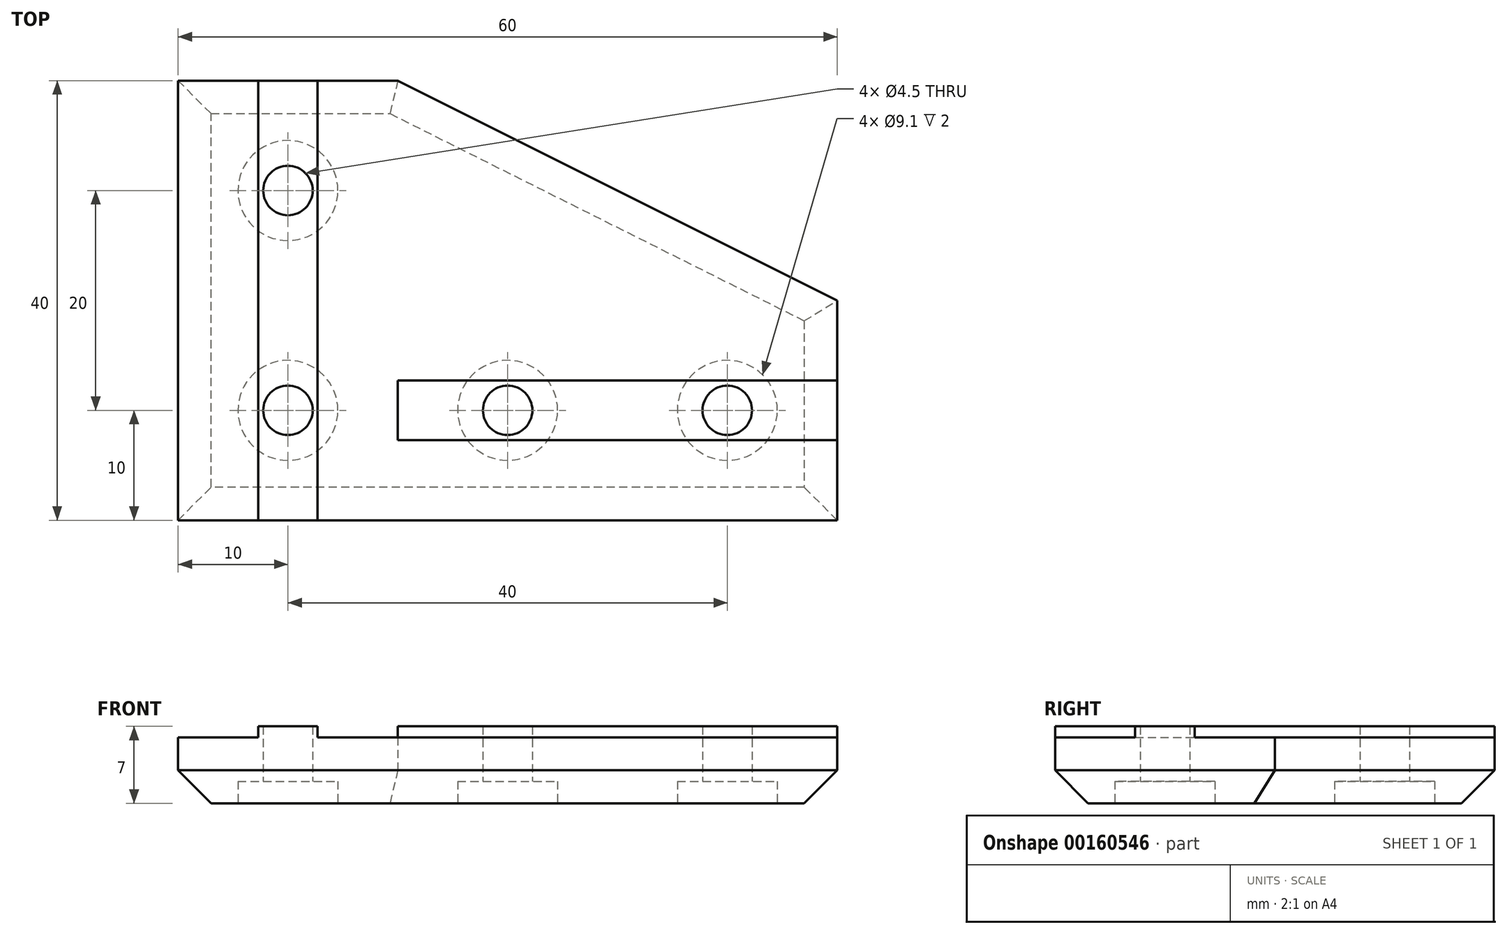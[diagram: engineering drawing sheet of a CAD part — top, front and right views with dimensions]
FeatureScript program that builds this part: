
annotation { "Feature Type Name" : "Feature", "Feature Type Description" : "" }
export const myFeature = defineFeature(function(context is Context, id is Id, definition is map)
    precondition{}
    {
        {
            var Q0;
            Q0=qCreatedBy(makeId("Top.planeOp"),FACE);
            var sketch = newSketch(context, id + "F0", { "sketchPlane" : qUnion([Q0])});
            skLineSegment(sketch, "E0", {"start": v(0, 0) * mm, "end": v(0, 40) * mm});
            skLineSegment(sketch, "E1", {"start": v(0, 40) * mm, "end": v(20, 40) * mm});
            skLineSegment(sketch, "E2", {"start": v(20, 40) * mm, "end": v(20, 20) * mm, "construction": true});
            skLineSegment(sketch, "E3", {"start": v(20, 20) * mm, "end": v(60, 20) * mm, "construction": true});
            skLineSegment(sketch, "E4", {"start": v(60, 20) * mm, "end": v(60, 0) * mm});
            skLineSegment(sketch, "E5", {"start": v(60, 0) * mm, "end": v(0, 0) * mm});
            skLineSegment(sketch, "E6", {"start": v(20, 40) * mm, "end": v(60, 20) * mm});
            skSolve(sketch);
        }
        {
            var Q0;
            Q0=qSketchRegion(id+"F0",true);
            extrude(context, id + "F1", {"entities" : qUnion([Q0]), "depth" : 6 * mm});
        }
        {
            var Q0;
            Q0=makeQuery(id+"F1.opExtrude","CAP_FACE",FACE,{"disambiguationData":[OSD([sQuery(id+"F0.wireOp",EDGE,"E0"),sQuery(id+"F0.wireOp",EDGE,"E1"),sQuery(id+"F0.wireOp",EDGE,"E2"),sQuery(id+"F0.wireOp",EDGE,"E3"),sQuery(id+"F0.wireOp",EDGE,"E4"),sQuery(id+"F0.wireOp",EDGE,"E5")])],"isStart":false});
            var sketch = newSketch(context, id + "F2", { "sketchPlane" : qUnion([Q0])});
            skLineSegment(sketch, "E7", {"start": v(7.3, 40) * mm, "end": v(12.71, 40) * mm});
            skLineSegment(sketch, "E8", {"start": v(12.71, 40) * mm, "end": v(12.71, 0) * mm});
            skLineSegment(sketch, "E9", {"start": v(12.71, 0) * mm, "end": v(10, 0) * mm});
            skPoint(sketch, "E9.endSnap0", {"position": v(10, 40) * mm});
            skLineSegment(sketch, "E10", {"start": v(10, 0) * mm, "end": v(7.3, 0) * mm});
            skLineSegment(sketch, "E11", {"start": v(7.3, 0) * mm, "end": v(7.3, 40) * mm});
            skLineSegment(sketch, "E12", {"start": v(60, 12.7) * mm, "end": v(60, 7.3) * mm});
            skLineSegment(sketch, "E13", {"start": v(60, 7.3) * mm, "end": v(20, 7.3) * mm});
            skLineSegment(sketch, "E14", {"start": v(20, 7.3) * mm, "end": v(20, 10) * mm});
            skPoint(sketch, "E14.endSnap0", {"position": v(60, 10) * mm});
            skLineSegment(sketch, "E15", {"start": v(20, 10) * mm, "end": v(20, 12.71) * mm});
            skLineSegment(sketch, "E16", {"start": v(20, 12.71) * mm, "end": v(60, 12.71) * mm});
            skSolve(sketch);
        }
        {
            var Q0;
            Q0=qSketchRegion(id+"F2",true);
            extrude(context, id + "F3", {"entities" : qUnion([Q0]), "operationType" : NewBodyOperationType.ADD, "flatOperationType" : FlatOperationType.REMOVE, "offsetDistance" : 25 * mm, "depth" : 1 * mm, "domain" : OperationDomain.MODEL});
        }
        {
            var Q0;
            Q0=makeQuery(id+"F1.opExtrude","CAP_FACE",FACE,{"disambiguationData":[OSD([sQuery(id+"F0.wireOp",EDGE,"E0"),sQuery(id+"F0.wireOp",EDGE,"E1"),sQuery(id+"F0.wireOp",EDGE,"E2"),sQuery(id+"F0.wireOp",EDGE,"E3"),sQuery(id+"F0.wireOp",EDGE,"E4"),sQuery(id+"F0.wireOp",EDGE,"E5")])],"isStart":true});
            var sketch = newSketch(context, id + "F4", { "sketchPlane" : qUnion([Q0])});
            skCircle(sketch, "E17", {"center": v(10, -10) * mm, "radius": 2.25 * mm});
            skCircle(sketch, "E18", {"center": v(50, -10) * mm, "radius": 2.25 * mm});
            skCircle(sketch, "E19", {"center": v(10, -30) * mm, "radius": 2.25 * mm});
            skCircle(sketch, "E20", {"center": v(30, -10) * mm, "radius": 2.25 * mm});
            skSolve(sketch);
        }
        {
            var Q0;
            Q0=qSketchRegion(id+"F4",true);
            extrude(context, id + "F5", {"entities" : qUnion([Q0]), "operationType" : NewBodyOperationType.REMOVE, "endBound" : BoundingType.THROUGH_ALL, "oppositeDirection" : true, "depth" : 25 * mm});
        }
        {
            var Q0;
            Q0=makeQuery(id+"F1.opExtrude","CAP_FACE",FACE,{"disambiguationData":[OSD([sQuery(id+"F0.wireOp",EDGE,"E0"),sQuery(id+"F0.wireOp",EDGE,"E1"),sQuery(id+"F0.wireOp",EDGE,"E2"),sQuery(id+"F0.wireOp",EDGE,"E3"),sQuery(id+"F0.wireOp",EDGE,"E4"),sQuery(id+"F0.wireOp",EDGE,"E5")])],"isStart":true});
            var sketch = newSketch(context, id + "F6", { "sketchPlane" : qUnion([Q0])});
            skCircle(sketch, "E21", {"center": v(10, -10) * mm, "radius": 4.55 * mm});
            skCircle(sketch, "E22", {"center": v(30, -10) * mm, "radius": 4.55 * mm});
            skCircle(sketch, "E23", {"center": v(50, -10) * mm, "radius": 4.55 * mm});
            skCircle(sketch, "E24", {"center": v(10, -30) * mm, "radius": 4.55 * mm});
            skSolve(sketch);
        }
        {
            var Q0;
            Q0=qSketchRegion(id+"F6",true);
            extrude(context, id + "F7", {"entities" : qUnion([Q0]), "operationType" : NewBodyOperationType.REMOVE, "oppositeDirection" : true, "depth" : 2 * mm});
        }
        {
            var Q0;
            Q0=makeQuery(id+"F1.opExtrude","CAP_EDGE",EDGE,{"disambiguationData":[OSD([sQuery(id+"F0.wireOp",EDGE,"E5")])],"isStart":true});
            var Q1;
            Q1=makeQuery(id+"F1.opExtrude","CAP_EDGE",EDGE,{"disambiguationData":[OSD([sQuery(id+"F0.wireOp",EDGE,"E0")])],"isStart":true});
            var Q2;
            Q2=makeQuery(id+"F1.opExtrude","CAP_EDGE",EDGE,{"disambiguationData":[OSD([sQuery(id+"F0.wireOp",EDGE,"E2")])],"isStart":true});
            var Q3;
            Q3=makeQuery(id+"F1.opExtrude","CAP_EDGE",EDGE,{"disambiguationData":[OSD([sQuery(id+"F0.wireOp",EDGE,"E3")])],"isStart":true});
            var Q4;
            Q4=makeQuery(id+"F1.opExtrude","CAP_EDGE",EDGE,{"disambiguationData":[OSD([sQuery(id+"F0.wireOp",EDGE,"E4")])],"isStart":true});
            var Q5;
            Q5=makeQuery(id+"F1.opExtrude","CAP_EDGE",EDGE,{"disambiguationData":[OSD([sQuery(id+"F0.wireOp",EDGE,"E1")])],"isStart":true});
            var Q6;
            Q6=makeQuery(id+"F1.opExtrude","CAP_EDGE",EDGE,{"disambiguationData":[OSD([sQuery(id+"F0.wireOp",EDGE,"E6")])],"isStart":true});
            chamfer(context, id + "F8", {"entities" : qUnion([Q0, Q1, Q2, Q3, Q4, Q5, Q6]), "width" : 3 * mm, "tangentPropagation" : true});
        }
    });
